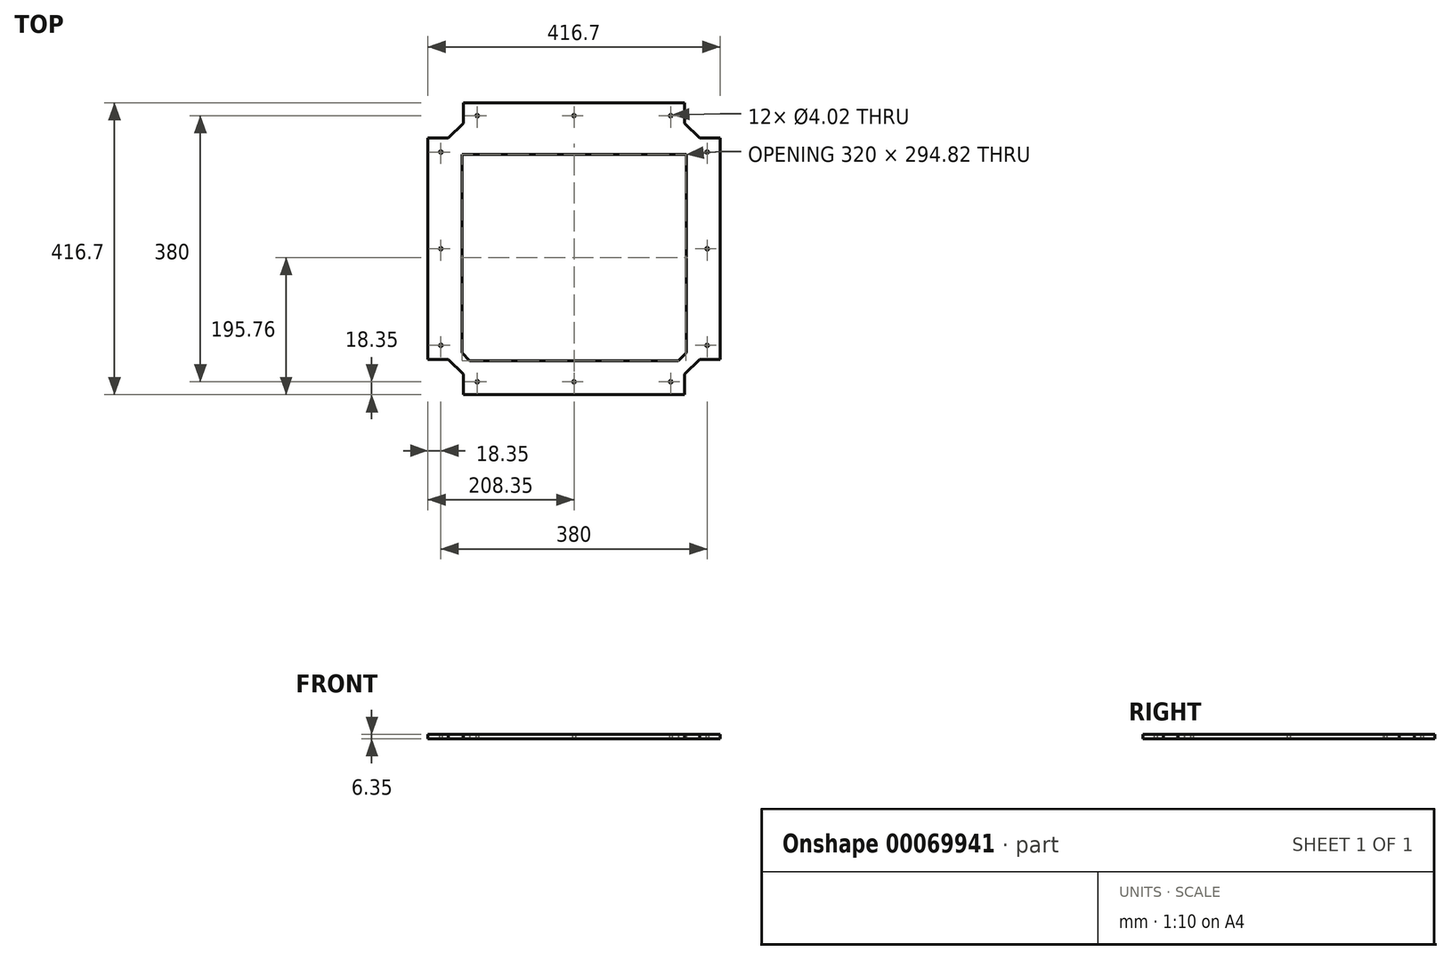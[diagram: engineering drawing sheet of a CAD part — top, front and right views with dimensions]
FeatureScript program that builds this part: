
annotation { "Feature Type Name" : "Feature", "Feature Type Description" : "" }
export const myFeature = defineFeature(function(context is Context, id is Id, definition is map)
    precondition{}
    {
        {
            var Q0;
            Q0=qCreatedBy(makeId("Top.planeOp"),FACE);
            var sketch = newSketch(context, id + "F0", { "sketchPlane" : qUnion([Q0])});
            skLineSegment(sketch, "E0", {"start": v(0, 0) * mm, "end": v(0, 180) * mm, "construction": true});
            skLineSegment(sketch, "E1", {"start": v(0, 180) * mm, "end": v(160, 180) * mm, "construction": true});
            skLineSegment(sketch, "E2", {"start": v(160, 180) * mm, "end": v(180, 160) * mm, "construction": true});
            skLineSegment(sketch, "E3", {"start": v(180, 160) * mm, "end": v(180, 0) * mm, "construction": true});
            skLineSegment(sketch, "E4", {"start": v(180, 0) * mm, "end": v(180, -160) * mm, "construction": true});
            skLineSegment(sketch, "E5", {"start": v(180, -160) * mm, "end": v(160, -180) * mm, "construction": true});
            skLineSegment(sketch, "E6", {"start": v(160, -180) * mm, "end": v(0, -180) * mm, "construction": true});
            skLineSegment(sketch, "E7", {"start": v(0, -180) * mm, "end": v(-160, -180) * mm, "construction": true});
            skLineSegment(sketch, "E8", {"start": v(-160, -180) * mm, "end": v(-180, -160) * mm, "construction": true});
            skLineSegment(sketch, "E9", {"start": v(-180, -160) * mm, "end": v(-180, 0) * mm, "construction": true});
            skLineSegment(sketch, "E10", {"start": v(-180, 0) * mm, "end": v(-180, 160) * mm, "construction": true});
            skLineSegment(sketch, "E11", {"start": v(-180, 160) * mm, "end": v(-160, 180) * mm, "construction": true});
            skLineSegment(sketch, "E12", {"start": v(-160, 180) * mm, "end": v(0, 180) * mm, "construction": true});
            skLineSegment(sketch, "E13", {"start": v(-180, 0) * mm, "end": v(0, 0) * mm, "construction": true});
            skLineSegment(sketch, "E14", {"start": v(0, 0) * mm, "end": v(180, 0) * mm, "construction": true});
            skLineSegment(sketch, "E15", {"start": v(0, 0) * mm, "end": v(0, -180) * mm, "construction": true});
            skLineSegment(sketch, "E16", {"start": v(-160, 180) * mm, "end": v(-160, 208.35) * mm, "construction": true});
            skLineSegment(sketch, "E17", {"start": v(-180, 160) * mm, "end": v(-208.35, 160) * mm, "construction": true});
            skLineSegment(sketch, "E18", {"start": v(160, 180) * mm, "end": v(160, 208.35) * mm, "construction": true});
            skLineSegment(sketch, "E19", {"start": v(180, 160) * mm, "end": v(208.35, 160) * mm, "construction": true});
            skLineSegment(sketch, "E20", {"start": v(180, -160) * mm, "end": v(208.35, -160) * mm, "construction": true});
            skLineSegment(sketch, "E21", {"start": v(160, -180) * mm, "end": v(160, -208.35) * mm, "construction": true});
            skLineSegment(sketch, "E22", {"start": v(-180, -160) * mm, "end": v(-208.35, -160) * mm, "construction": true});
            skLineSegment(sketch, "E23", {"start": v(-160, -180) * mm, "end": v(-160, -208.35) * mm, "construction": true});
            skLineSegment(sketch, "E24", {"start": v(-160, 194.17) * mm, "end": v(-158, 194.17) * mm, "construction": true});
            skLineSegment(sketch, "E25", {"start": v(-170, 170) * mm, "end": v(-168.59, 168.59) * mm, "construction": true});
            skLineSegment(sketch, "E26", {"start": v(-194.17, 160) * mm, "end": v(-194.17, 158) * mm, "construction": true});
            skLineSegment(sketch, "E27", {"start": v(160, 194.17) * mm, "end": v(158, 194.17) * mm, "construction": true});
            skLineSegment(sketch, "E28", {"start": v(170, 170) * mm, "end": v(168.59, 168.59) * mm, "construction": true});
            skLineSegment(sketch, "E29", {"start": v(194.17, 160) * mm, "end": v(194.17, 158) * mm, "construction": true});
            skLineSegment(sketch, "E30", {"start": v(194.17, -160) * mm, "end": v(194.17, -158) * mm, "construction": true});
            skLineSegment(sketch, "E31", {"start": v(170, -170) * mm, "end": v(168.59, -168.59) * mm, "construction": true});
            skLineSegment(sketch, "E32", {"start": v(160, -194.17) * mm, "end": v(158, -194.17) * mm, "construction": true});
            skLineSegment(sketch, "E33", {"start": v(-194.17, -160) * mm, "end": v(-194.17, -158) * mm, "construction": true});
            skLineSegment(sketch, "E34", {"start": v(-160, -194.18) * mm, "end": v(-158, -194.18) * mm, "construction": true});
            skLineSegment(sketch, "E35", {"start": v(-170, -170) * mm, "end": v(-168.59, -168.59) * mm, "construction": true});
            skLineSegment(sketch, "E36", {"start": v(-158, 194.17) * mm, "end": v(-158, 208.35) * mm});
            skLineSegment(sketch, "E37", {"start": v(-158, 208.35) * mm, "end": v(158, 208.35) * mm});
            skLineSegment(sketch, "E38", {"start": v(158, 208.35) * mm, "end": v(158, 194.17) * mm});
            skLineSegment(sketch, "E39", {"start": v(158, 194.17) * mm, "end": v(158, 179.17) * mm});
            skLineSegment(sketch, "E40", {"start": v(168.59, 168.59) * mm, "end": v(158, 179.17) * mm});
            skLineSegment(sketch, "E41", {"start": v(168.59, 168.59) * mm, "end": v(179.17, 158) * mm});
            skLineSegment(sketch, "E42", {"start": v(194.17, 158) * mm, "end": v(179.17, 158) * mm});
            skLineSegment(sketch, "E43", {"start": v(194.17, 158) * mm, "end": v(208.35, 158) * mm});
            skLineSegment(sketch, "E44", {"start": v(208.35, 158) * mm, "end": v(208.35, -158) * mm});
            skLineSegment(sketch, "E45", {"start": v(208.35, -158) * mm, "end": v(194.17, -158) * mm});
            skLineSegment(sketch, "E46", {"start": v(194.17, -158) * mm, "end": v(179.17, -158) * mm});
            skLineSegment(sketch, "E47", {"start": v(-208.35, 158) * mm, "end": v(-194.17, 158) * mm});
            skLineSegment(sketch, "E48", {"start": v(-194.17, 158) * mm, "end": v(-179.17, 158) * mm});
            skLineSegment(sketch, "E49", {"start": v(-208.35, 158) * mm, "end": v(-208.35, -158) * mm});
            skLineSegment(sketch, "E50", {"start": v(-208.35, -158) * mm, "end": v(-194.17, -158) * mm});
            skLineSegment(sketch, "E51", {"start": v(-194.17, -158) * mm, "end": v(-179.17, -158) * mm});
            skLineSegment(sketch, "E52", {"start": v(-168.59, -168.59) * mm, "end": v(-179.17, -158) * mm});
            skLineSegment(sketch, "E53", {"start": v(-168.59, -168.59) * mm, "end": v(-158, -179.17) * mm});
            skLineSegment(sketch, "E54", {"start": v(-158, -208.35) * mm, "end": v(-158, -194.18) * mm});
            skLineSegment(sketch, "E55", {"start": v(-158, -194.18) * mm, "end": v(-158, -179.17) * mm});
            skLineSegment(sketch, "E56", {"start": v(-158, -208.35) * mm, "end": v(158, -208.35) * mm});
            skLineSegment(sketch, "E57", {"start": v(158, -208.35) * mm, "end": v(158, -194.17) * mm});
            skLineSegment(sketch, "E58", {"start": v(158, -194.17) * mm, "end": v(158, -179.17) * mm});
            skLineSegment(sketch, "E59", {"start": v(168.59, -168.59) * mm, "end": v(158, -179.17) * mm});
            skLineSegment(sketch, "E60", {"start": v(168.59, -168.59) * mm, "end": v(179.17, -158) * mm});
            skLineSegment(sketch, "E61", {"start": v(-168.59, 168.59) * mm, "end": v(-179.17, 158) * mm});
            skLineSegment(sketch, "E62", {"start": v(-168.59, 168.59) * mm, "end": v(-158, 179.17) * mm});
            skLineSegment(sketch, "E63", {"start": v(-158, 194.17) * mm, "end": v(-158, 179.17) * mm});
            skLineSegment(sketch, "E64", {"start": v(-180, 0) * mm, "end": v(-190, 0) * mm, "construction": true});
            skLineSegment(sketch, "E65", {"start": v(-190, 0) * mm, "end": v(-190, 158) * mm, "construction": true});
            skLineSegment(sketch, "E66", {"start": v(-190, 0) * mm, "end": v(-190, -158) * mm, "construction": true});
            skPoint(sketch, "E66.endSnap0", {"position": v(-186.67, -158) * mm});
            skCircle(sketch, "E67", {"center": v(-190, -138) * mm, "radius": 2 * mm});
            skCircle(sketch, "E68", {"center": v(-190, 0) * mm, "radius": 2 * mm});
            skCircle(sketch, "E69", {"center": v(-190, 138) * mm, "radius": 2 * mm});
            skLineSegment(sketch, "E70", {"start": v(0, 180) * mm, "end": v(0, 190) * mm, "construction": true});
            skCircle(sketch, "E71", {"center": v(0, 190) * mm, "radius": 2 * mm});
            skCircle(sketch, "E72", {"center": v(-138, 190) * mm, "radius": 2 * mm});
            skCircle(sketch, "E73", {"center": v(138, 190) * mm, "radius": 2 * mm});
            skLineSegment(sketch, "E74", {"start": v(180, 0) * mm, "end": v(190, 0) * mm, "construction": true});
            skCircle(sketch, "E75", {"center": v(190, 0) * mm, "radius": 2 * mm});
            skCircle(sketch, "E76", {"center": v(190, -138) * mm, "radius": 2 * mm});
            skCircle(sketch, "E77", {"center": v(190, 138) * mm, "radius": 2 * mm});
            skLineSegment(sketch, "E78", {"start": v(0, -180) * mm, "end": v(0, -190) * mm, "construction": true});
            skCircle(sketch, "E79", {"center": v(0, -190) * mm, "radius": 2 * mm});
            skCircle(sketch, "E80", {"center": v(-138, -190) * mm, "radius": 2 * mm});
            skCircle(sketch, "E81", {"center": v(138, -190) * mm, "radius": 2 * mm});
            skLineSegment(sketch, "E82", {"start": v(-168.59, -168.59) * mm, "end": v(-154.44, -154.44) * mm, "construction": true});
            skLineSegment(sketch, "E83", {"start": v(168.59, -168.59) * mm, "end": v(154.44, -154.44) * mm, "construction": true});
            skLineSegment(sketch, "E84", {"start": v(154.44, -154.44) * mm, "end": v(160, -148.89) * mm});
            skLineSegment(sketch, "E85", {"start": v(154.44, -154.44) * mm, "end": v(148.89, -160) * mm});
            skLineSegment(sketch, "E86", {"start": v(-154.44, -154.44) * mm, "end": v(-148.89, -160) * mm});
            skLineSegment(sketch, "E87", {"start": v(-154.44, -154.44) * mm, "end": v(-160, -148.89) * mm});
            skLineSegment(sketch, "E88.trimOffspring", {"start": v(-160, -148.89) * mm, "end": v(-160, 134.75) * mm});
            skPoint(sketch, "E89.orphan", {"position": v(-168.59, -160) * mm});
            skLineSegment(sketch, "E90.trimOffspring", {"start": v(148.89, -160) * mm, "end": v(-148.89, -160) * mm});
            skPoint(sketch, "E91.orphan", {"position": v(160, -170) * mm});
            skLineSegment(sketch, "E92", {"start": v(160, -148.89) * mm, "end": v(160, 134.82) * mm});
            skLineSegment(sketch, "E93", {"start": v(-160, 134.75) * mm, "end": v(160, 134.82) * mm});
            skSolve(sketch);
        }
        {
            var Q0;
            Q0=makeQuery(id+"F0.imprint","IMPRINT",FACE,{"disambiguationData":[TD([[makeQuery(id+"F0.imprint","IMPRINT",EDGE,{"derivedFrom":sQuery(id+"F0.wireOp",EDGE,"E36")}),-1.0]])]});
            extrude(context, id + "F1", {"entities" : qUnion([Q0]), "depth" : 6.35 * mm});
        }
    });
